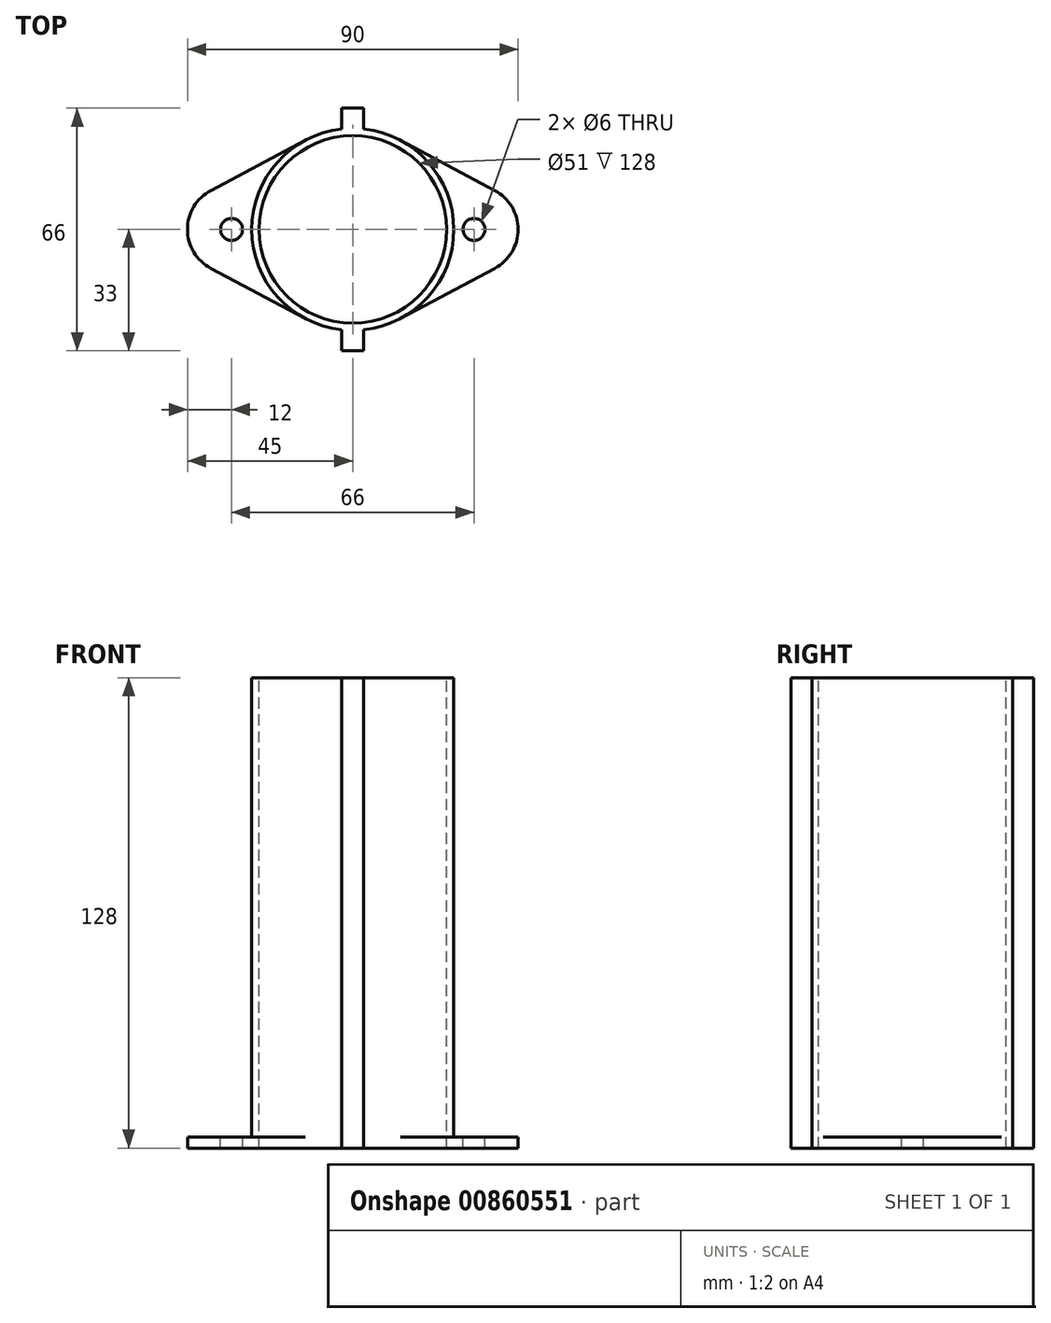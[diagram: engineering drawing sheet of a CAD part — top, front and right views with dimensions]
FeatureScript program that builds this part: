
annotation { "Feature Type Name" : "Feature", "Feature Type Description" : "" }
export const myFeature = defineFeature(function(context is Context, id is Id, definition is map)
    precondition{}
    {
        {
            var Q0;
            Q0=qCreatedBy(makeId("Top.planeOp"),FACE);
            var sketch = newSketch(context, id + "F0", { "sketchPlane" : qUnion([Q0])});
            skPoint(sketch, "E0", {"position": v(-33, 0) * mm});
            skPoint(sketch, "E1", {"position": v(33, 0) * mm});
            skCircle(sketch, "E2", {"center": v(-33, 0) * mm, "radius": 3 * mm});
            skCircle(sketch, "E3", {"center": v(33, 0) * mm, "radius": 3 * mm});
            skCircle(sketch, "E4", {"center": v(0, 0) * mm, "radius": 27.5 * mm});
            skCircle(sketch, "E5", {"center": v(-33, 0) * mm, "radius": 12 * mm});
            skCircle(sketch, "E6", {"center": v(33, 0) * mm, "radius": 12 * mm});
            skLineSegment(sketch, "E7", {"start": v(-44.55, 7.45) * mm, "end": v(-7.38, 27.22) * mm});
            skLineSegment(sketch, "E8", {"start": v(8.05, 26.87) * mm, "end": v(44.27, 7.6) * mm});
            skLineSegment(sketch, "E9", {"start": v(-44.37, -7.54) * mm, "end": v(-9.32, -26.19) * mm});
            skLineSegment(sketch, "E10", {"start": v(44, -7.74) * mm, "end": v(9.39, -26.15) * mm});
            skCircle(sketch, "E11", {"center": v(0, 0) * mm, "radius": 25.5 * mm});
            skLineSegment(sketch, "E12.bottom", {"start": v(-3, 33) * mm, "end": v(3, 33) * mm});
            skLineSegment(sketch, "E12.top", {"start": v(-3, -33) * mm, "end": v(3, -33) * mm});
            skLineSegment(sketch, "E12.left", {"start": v(-3, 33) * mm, "end": v(-3, -33) * mm});
            skLineSegment(sketch, "E12.right", {"start": v(3, 33) * mm, "end": v(3, -33) * mm});
            skSolve(sketch);
        }
        {
            var Q0;
            {var subQ0=sQuery(id+"F0.wireOp",EDGE,"E8");var subQ1=sQuery(id+"F0.wireOp",EDGE,"E4");var subQ2=makeQuery(id+"F0.imprint","INTERSECT",VERTEX,{"derivedFrom":[subQ1,subQ0]});Q0=makeQuery(id+"F0.imprint","IMPRINT",FACE,{"disambiguationData":[TD([[makeQuery(id+"F0.imprint","IMPRINT",EDGE,{"disambiguationData":[TD([[subQ2,1.0]])],"derivedFrom":subQ1}),-1.0]])]});}
            var Q1;
            Q1=makeQuery(id+"F0.imprint","IMPRINT",FACE,{"disambiguationData":[TD([[makeQuery(id+"F0.imprint","IMPRINT",EDGE,{"derivedFrom":sQuery(id+"F0.wireOp",EDGE,"E3")}),-1.0]])]});
            var Q2;
            {var subQ0=sQuery(id+"F0.wireOp",EDGE,"E6");var subQ1=sQuery(id+"F0.wireOp",EDGE,"E4");var subQ2=makeQuery(id+"F0.imprint","INTERSECT",VERTEX,{"disambiguationData":[OD(0.0)],"derivedFrom":[subQ1,subQ0]});Q2=makeQuery(id+"F0.imprint","IMPRINT",FACE,{"disambiguationData":[TD([[makeQuery(id+"F0.imprint","IMPRINT",EDGE,{"disambiguationData":[TD([[subQ2,1.0]])],"derivedFrom":subQ1}),1.0]])]});}
            var Q3;
            {var subQ10=sQuery(id+"F0.wireOp",EDGE,"E12.bottom");Q3=makeQuery(id+"F0.imprint","IMPRINT",FACE,{"disambiguationData":[TD([[makeQuery(id+"F0.imprint","IMPRINT",EDGE,{"derivedFrom":subQ10}),1.0]])]});}
            var Q4;
            {var subQ0=sQuery(id+"F0.wireOp",EDGE,"E10");var subQ1=sQuery(id+"F0.wireOp",EDGE,"E4");var subQ2=makeQuery(id+"F0.imprint","INTERSECT",VERTEX,{"derivedFrom":[subQ1,subQ0]});Q4=makeQuery(id+"F0.imprint","IMPRINT",FACE,{"disambiguationData":[TD([[makeQuery(id+"F0.imprint","IMPRINT",EDGE,{"disambiguationData":[TD([[subQ2,-1.0]])],"derivedFrom":subQ1}),-1.0]])]});}
            var Q5;
            {var subQ1=sQuery(id+"F0.wireOp",EDGE,"uCnmd3xf-1DHz-8HX0-QWDX-xBedthpKxEkq.bottom");Q5=makeQuery(id+"F0.imprint","IMPRINT",FACE,{"disambiguationData":[TD([[makeQuery(id+"F0.imprint","IMPRINT",EDGE,{"derivedFrom":subQ1}),1.0]])]});}
            var Q6;
            {var subQ0=sQuery(id+"F0.wireOp",EDGE,"E12.left");var subQ1=sQuery(id+"F0.wireOp",EDGE,"W2dtvIMr-H2jL-05E6-sB4P-pdGcn9n6LOdG");var subQ2=makeQuery(id+"F0.imprint","INTERSECT",VERTEX,{"disambiguationData":[OD(0.0)],"derivedFrom":[subQ1,subQ0]});Q6=makeQuery(id+"F0.imprint","IMPRINT",FACE,{"disambiguationData":[TD([[makeQuery(id+"F0.imprint","IMPRINT",EDGE,{"disambiguationData":[TD([[subQ2,-1.0]])],"derivedFrom":subQ1}),-1.0]])]});}
            var Q7;
            {var subQ5=sQuery(id+"F0.wireOp",EDGE,"uCnmd3xf-1DHz-8HX0-QWDX-xBedthpKxEkq.bottom");Q7=makeQuery(id+"F0.imprint","IMPRINT",FACE,{"disambiguationData":[TD([[makeQuery(id+"F0.imprint","IMPRINT",EDGE,{"derivedFrom":subQ5}),-1.0]])]});}
            var Q8;
            {var subQ0=sQuery(id+"F0.wireOp",EDGE,"uCnmd3xf-1DHz-8HX0-QWDX-xBedthpKxEkq.right");var subQ1=sQuery(id+"F0.wireOp",EDGE,"W2dtvIMr-H2jL-05E6-sB4P-pdGcn9n6LOdG");var subQ2=makeQuery(id+"F0.imprint","INTERSECT",VERTEX,{"disambiguationData":[OD(0.0)],"derivedFrom":[subQ1,subQ0]});Q8=makeQuery(id+"F0.imprint","IMPRINT",FACE,{"disambiguationData":[TD([[makeQuery(id+"F0.imprint","IMPRINT",EDGE,{"disambiguationData":[TD([[subQ2,-1.0]])],"derivedFrom":subQ1}),-1.0]])]});}
            var Q9;
            {var subQ0=sQuery(id+"F0.wireOp",EDGE,"uCnmd3xf-1DHz-8HX0-QWDX-xBedthpKxEkq.left");var subQ1=sQuery(id+"F0.wireOp",EDGE,"W2dtvIMr-H2jL-05E6-sB4P-pdGcn9n6LOdG");var subQ2=makeQuery(id+"F0.imprint","INTERSECT",VERTEX,{"disambiguationData":[OD(0.0)],"derivedFrom":[subQ1,subQ0]});Q9=makeQuery(id+"F0.imprint","IMPRINT",FACE,{"disambiguationData":[TD([[makeQuery(id+"F0.imprint","IMPRINT",EDGE,{"disambiguationData":[TD([[subQ2,-1.0]])],"derivedFrom":subQ1}),-1.0]])]});}
            var Q10;
            {var subQ0=sQuery(id+"F0.wireOp",EDGE,"82vNiPyT-JWAm-ZdGo-BXKd-8rWHJqwmHx42.bottom");var subQ1=sQuery(id+"F0.wireOp",EDGE,"W2dtvIMr-H2jL-05E6-sB4P-pdGcn9n6LOdG");var subQ2=makeQuery(id+"F0.imprint","INTERSECT",VERTEX,{"disambiguationData":[OD(0.0)],"derivedFrom":[subQ1,subQ0]});Q10=makeQuery(id+"F0.imprint","IMPRINT",FACE,{"disambiguationData":[TD([[makeQuery(id+"F0.imprint","IMPRINT",EDGE,{"disambiguationData":[TD([[subQ2,-1.0]])],"derivedFrom":subQ1}),-1.0]])]});}
            var Q11;
            {var subQ0=sQuery(id+"F0.wireOp",EDGE,"E12.right");var subQ1=sQuery(id+"F0.wireOp",EDGE,"W2dtvIMr-H2jL-05E6-sB4P-pdGcn9n6LOdG");var subQ2=makeQuery(id+"F0.imprint","INTERSECT",VERTEX,{"disambiguationData":[OD(0.0)],"derivedFrom":[subQ1,subQ0]});Q11=makeQuery(id+"F0.imprint","IMPRINT",FACE,{"disambiguationData":[TD([[makeQuery(id+"F0.imprint","IMPRINT",EDGE,{"disambiguationData":[TD([[subQ2,-1.0]])],"derivedFrom":subQ1}),-1.0]])]});}
            var Q12;
            {var subQ0=sQuery(id+"F0.wireOp",EDGE,"82vNiPyT-JWAm-ZdGo-BXKd-8rWHJqwmHx42.bottom");var subQ1=sQuery(id+"F0.wireOp",EDGE,"W2dtvIMr-H2jL-05E6-sB4P-pdGcn9n6LOdG");var subQ2=makeQuery(id+"F0.imprint","INTERSECT",VERTEX,{"disambiguationData":[OD(1.0)],"derivedFrom":[subQ1,subQ0]});Q12=makeQuery(id+"F0.imprint","IMPRINT",FACE,{"disambiguationData":[TD([[makeQuery(id+"F0.imprint","IMPRINT",EDGE,{"disambiguationData":[TD([[subQ2,-1.0]])],"derivedFrom":subQ1}),-1.0]])]});}
            var Q13;
            {var subQ0=sQuery(id+"F0.wireOp",EDGE,"kkNvgBHZ-zSj7-8Lj1-WI96-c3132SsyxNSe.bottom");var subQ1=sQuery(id+"F0.wireOp",EDGE,"W2dtvIMr-H2jL-05E6-sB4P-pdGcn9n6LOdG");var subQ2=makeQuery(id+"F0.imprint","INTERSECT",VERTEX,{"disambiguationData":[OD(1.0)],"derivedFrom":[subQ1,subQ0]});Q13=makeQuery(id+"F0.imprint","IMPRINT",FACE,{"disambiguationData":[TD([[makeQuery(id+"F0.imprint","IMPRINT",EDGE,{"disambiguationData":[TD([[subQ2,-1.0]])],"derivedFrom":subQ1}),-1.0]])]});}
            var Q14;
            {var subQ5=sQuery(id+"F0.wireOp",EDGE,"kkNvgBHZ-zSj7-8Lj1-WI96-c3132SsyxNSe.left");Q14=makeQuery(id+"F0.imprint","IMPRINT",FACE,{"disambiguationData":[TD([[makeQuery(id+"F0.imprint","IMPRINT",EDGE,{"derivedFrom":subQ5}),1.0]])]});}
            var Q15;
            {var subQ0=sQuery(id+"F0.wireOp",EDGE,"kkNvgBHZ-zSj7-8Lj1-WI96-c3132SsyxNSe.left");Q15=makeQuery(id+"F0.imprint","IMPRINT",FACE,{"disambiguationData":[TD([[makeQuery(id+"F0.imprint","IMPRINT",EDGE,{"derivedFrom":subQ0}),-1.0]])]});}
            var Q16;
            {var subQ0=sQuery(id+"F0.wireOp",EDGE,"kkNvgBHZ-zSj7-8Lj1-WI96-c3132SsyxNSe.top");var subQ1=sQuery(id+"F0.wireOp",EDGE,"W2dtvIMr-H2jL-05E6-sB4P-pdGcn9n6LOdG");var subQ2=makeQuery(id+"F0.imprint","INTERSECT",VERTEX,{"disambiguationData":[OD(0.0)],"derivedFrom":[subQ1,subQ0]});Q16=makeQuery(id+"F0.imprint","IMPRINT",FACE,{"disambiguationData":[TD([[makeQuery(id+"F0.imprint","IMPRINT",EDGE,{"disambiguationData":[TD([[subQ2,-1.0]])],"derivedFrom":subQ1}),-1.0]])]});}
            var Q17;
            {var subQ0=sQuery(id+"F0.wireOp",EDGE,"kkNvgBHZ-zSj7-8Lj1-WI96-c3132SsyxNSe.right");Q17=makeQuery(id+"F0.imprint","IMPRINT",FACE,{"disambiguationData":[TD([[makeQuery(id+"F0.imprint","IMPRINT",EDGE,{"derivedFrom":subQ0}),1.0]])]});}
            var Q18;
            {var subQ0=sQuery(id+"F0.wireOp",EDGE,"82vNiPyT-JWAm-ZdGo-BXKd-8rWHJqwmHx42.bottom");var subQ1=sQuery(id+"F0.wireOp",EDGE,"W2dtvIMr-H2jL-05E6-sB4P-pdGcn9n6LOdG");var subQ2=makeQuery(id+"F0.imprint","INTERSECT",VERTEX,{"disambiguationData":[OD(0.0)],"derivedFrom":[subQ1,subQ0]});Q18=makeQuery(id+"F0.imprint","IMPRINT",FACE,{"disambiguationData":[TD([[makeQuery(id+"F0.imprint","IMPRINT",EDGE,{"disambiguationData":[TD([[subQ2,1.0]])],"derivedFrom":subQ1}),-1.0]])]});}
            var Q19;
            {var subQ0=sQuery(id+"F0.wireOp",EDGE,"kkNvgBHZ-zSj7-8Lj1-WI96-c3132SsyxNSe.bottom");var subQ1=sQuery(id+"F0.wireOp",EDGE,"W2dtvIMr-H2jL-05E6-sB4P-pdGcn9n6LOdG");var subQ2=makeQuery(id+"F0.imprint","INTERSECT",VERTEX,{"disambiguationData":[OD(0.0)],"derivedFrom":[subQ1,subQ0]});Q19=makeQuery(id+"F0.imprint","IMPRINT",FACE,{"disambiguationData":[TD([[makeQuery(id+"F0.imprint","IMPRINT",EDGE,{"disambiguationData":[TD([[subQ2,1.0]])],"derivedFrom":subQ1}),-1.0]])]});}
            var Q20;
            {var subQ5=sQuery(id+"F0.wireOp",EDGE,"kkNvgBHZ-zSj7-8Lj1-WI96-c3132SsyxNSe.right");Q20=makeQuery(id+"F0.imprint","IMPRINT",FACE,{"disambiguationData":[TD([[makeQuery(id+"F0.imprint","IMPRINT",EDGE,{"derivedFrom":subQ5}),-1.0]])]});}
            var Q21;
            {var subQ0=sQuery(id+"F0.wireOp",EDGE,"82vNiPyT-JWAm-ZdGo-BXKd-8rWHJqwmHx42.top");var subQ1=sQuery(id+"F0.wireOp",EDGE,"W2dtvIMr-H2jL-05E6-sB4P-pdGcn9n6LOdG");var subQ2=makeQuery(id+"F0.imprint","INTERSECT",VERTEX,{"disambiguationData":[OD(1.0)],"derivedFrom":[subQ1,subQ0]});Q21=makeQuery(id+"F0.imprint","IMPRINT",FACE,{"disambiguationData":[TD([[makeQuery(id+"F0.imprint","IMPRINT",EDGE,{"disambiguationData":[TD([[subQ2,-1.0]])],"derivedFrom":subQ1}),-1.0]])]});}
            var Q22;
            {var subQ0=sQuery(id+"F0.wireOp",EDGE,"E12.right");var subQ1=sQuery(id+"F0.wireOp",EDGE,"W2dtvIMr-H2jL-05E6-sB4P-pdGcn9n6LOdG");var subQ2=makeQuery(id+"F0.imprint","INTERSECT",VERTEX,{"disambiguationData":[OD(1.0)],"derivedFrom":[subQ1,subQ0]});Q22=makeQuery(id+"F0.imprint","IMPRINT",FACE,{"disambiguationData":[TD([[makeQuery(id+"F0.imprint","IMPRINT",EDGE,{"disambiguationData":[TD([[subQ2,-1.0]])],"derivedFrom":subQ1}),-1.0]])]});}
            var Q23;
            {var subQ0=sQuery(id+"F0.wireOp",EDGE,"82vNiPyT-JWAm-ZdGo-BXKd-8rWHJqwmHx42.top");var subQ1=sQuery(id+"F0.wireOp",EDGE,"W2dtvIMr-H2jL-05E6-sB4P-pdGcn9n6LOdG");var subQ2=makeQuery(id+"F0.imprint","INTERSECT",VERTEX,{"disambiguationData":[OD(0.0)],"derivedFrom":[subQ1,subQ0]});Q23=makeQuery(id+"F0.imprint","IMPRINT",FACE,{"disambiguationData":[TD([[makeQuery(id+"F0.imprint","IMPRINT",EDGE,{"disambiguationData":[TD([[subQ2,-1.0]])],"derivedFrom":subQ1}),-1.0]])]});}
            var Q24;
            {var subQ0=sQuery(id+"F0.wireOp",EDGE,"uCnmd3xf-1DHz-8HX0-QWDX-xBedthpKxEkq.right");var subQ1=sQuery(id+"F0.wireOp",EDGE,"W2dtvIMr-H2jL-05E6-sB4P-pdGcn9n6LOdG");var subQ2=makeQuery(id+"F0.imprint","INTERSECT",VERTEX,{"disambiguationData":[OD(1.0)],"derivedFrom":[subQ1,subQ0]});Q24=makeQuery(id+"F0.imprint","IMPRINT",FACE,{"disambiguationData":[TD([[makeQuery(id+"F0.imprint","IMPRINT",EDGE,{"disambiguationData":[TD([[subQ2,-1.0]])],"derivedFrom":subQ1}),-1.0]])]});}
            var Q25;
            {var subQ0=sQuery(id+"F0.wireOp",EDGE,"uCnmd3xf-1DHz-8HX0-QWDX-xBedthpKxEkq.left");var subQ1=sQuery(id+"F0.wireOp",EDGE,"W2dtvIMr-H2jL-05E6-sB4P-pdGcn9n6LOdG");var subQ2=makeQuery(id+"F0.imprint","INTERSECT",VERTEX,{"disambiguationData":[OD(1.0)],"derivedFrom":[subQ1,subQ0]});Q25=makeQuery(id+"F0.imprint","IMPRINT",FACE,{"disambiguationData":[TD([[makeQuery(id+"F0.imprint","IMPRINT",EDGE,{"disambiguationData":[TD([[subQ2,-1.0]])],"derivedFrom":subQ1}),-1.0]])]});}
            var Q26;
            {var subQ0=sQuery(id+"F0.wireOp",EDGE,"E12.left");var subQ1=sQuery(id+"F0.wireOp",EDGE,"W2dtvIMr-H2jL-05E6-sB4P-pdGcn9n6LOdG");var subQ2=makeQuery(id+"F0.imprint","INTERSECT",VERTEX,{"disambiguationData":[OD(1.0)],"derivedFrom":[subQ1,subQ0]});Q26=makeQuery(id+"F0.imprint","IMPRINT",FACE,{"disambiguationData":[TD([[makeQuery(id+"F0.imprint","IMPRINT",EDGE,{"disambiguationData":[TD([[subQ2,-1.0]])],"derivedFrom":subQ1}),-1.0]])]});}
            var Q27;
            {var subQ1=sQuery(id+"F0.wireOp",EDGE,"uCnmd3xf-1DHz-8HX0-QWDX-xBedthpKxEkq.top");Q27=makeQuery(id+"F0.imprint","IMPRINT",FACE,{"disambiguationData":[TD([[makeQuery(id+"F0.imprint","IMPRINT",EDGE,{"derivedFrom":subQ1}),-1.0]])]});}
            var Q28;
            {var subQ5=sQuery(id+"F0.wireOp",EDGE,"uCnmd3xf-1DHz-8HX0-QWDX-xBedthpKxEkq.top");Q28=makeQuery(id+"F0.imprint","IMPRINT",FACE,{"disambiguationData":[TD([[makeQuery(id+"F0.imprint","IMPRINT",EDGE,{"derivedFrom":subQ5}),1.0]])]});}
            var Q29;
            {var subQ0=sQuery(id+"F0.wireOp",EDGE,"E7");var subQ1=sQuery(id+"F0.wireOp",EDGE,"E4");var subQ2=makeQuery(id+"F0.imprint","INTERSECT",VERTEX,{"derivedFrom":[subQ1,subQ0]});Q29=makeQuery(id+"F0.imprint","IMPRINT",FACE,{"disambiguationData":[TD([[makeQuery(id+"F0.imprint","IMPRINT",EDGE,{"disambiguationData":[TD([[subQ2,-1.0]])],"derivedFrom":subQ1}),-1.0]])]});}
            var Q30;
            Q30=makeQuery(id+"F0.imprint","IMPRINT",FACE,{"disambiguationData":[TD([[makeQuery(id+"F0.imprint","IMPRINT",EDGE,{"derivedFrom":sQuery(id+"F0.wireOp",EDGE,"E2")}),-1.0]])]});
            var Q31;
            {var subQ0=sQuery(id+"F0.wireOp",EDGE,"E5");var subQ1=sQuery(id+"F0.wireOp",EDGE,"E4");var subQ2=makeQuery(id+"F0.imprint","INTERSECT",VERTEX,{"disambiguationData":[OD(0.0)],"derivedFrom":[subQ1,subQ0]});Q31=makeQuery(id+"F0.imprint","IMPRINT",FACE,{"disambiguationData":[TD([[makeQuery(id+"F0.imprint","IMPRINT",EDGE,{"disambiguationData":[TD([[subQ2,-1.0]])],"derivedFrom":subQ1}),1.0]])]});}
            var Q32;
            {var subQ0=sQuery(id+"F0.wireOp",EDGE,"E9");var subQ1=sQuery(id+"F0.wireOp",EDGE,"E4");var subQ2=makeQuery(id+"F0.imprint","INTERSECT",VERTEX,{"derivedFrom":[subQ1,subQ0]});Q32=makeQuery(id+"F0.imprint","IMPRINT",FACE,{"disambiguationData":[TD([[makeQuery(id+"F0.imprint","IMPRINT",EDGE,{"disambiguationData":[TD([[subQ2,1.0]])],"derivedFrom":subQ1}),-1.0]])]});}
            var Q33;
            {var subQ5=sQuery(id+"F0.wireOp",EDGE,"E12.bottom");Q33=makeQuery(id+"F0.imprint","IMPRINT",FACE,{"disambiguationData":[TD([[makeQuery(id+"F0.imprint","IMPRINT",EDGE,{"derivedFrom":subQ5}),-1.0]])]});}
            var Q34;
            {var subQ0=sQuery(id+"F0.wireOp",EDGE,"E12.right");var subQ1=sQuery(id+"F0.wireOp",EDGE,"E4");var subQ2=makeQuery(id+"F0.imprint","INTERSECT",VERTEX,{"disambiguationData":[OD(0.0)],"derivedFrom":[subQ1,subQ0]});Q34=makeQuery(id+"F0.imprint","IMPRINT",FACE,{"disambiguationData":[TD([[makeQuery(id+"F0.imprint","IMPRINT",EDGE,{"disambiguationData":[TD([[subQ2,-1.0]])],"derivedFrom":subQ1}),1.0]])]});}
            var Q35;
            {var subQ0=sQuery(id+"F0.wireOp",EDGE,"E4");var subQ4=makeQuery(id+"F0.imprint","INTERSECT",VERTEX,{"derivedFrom":[subQ0,sQuery(id+"F0.wireOp",EDGE,"E8")]});Q35=makeQuery(id+"F0.imprint","IMPRINT",FACE,{"disambiguationData":[TD([[makeQuery(id+"F0.imprint","IMPRINT",EDGE,{"disambiguationData":[TD([[subQ4,1.0]])],"derivedFrom":subQ0}),1.0]])]});}
            var Q36;
            {var subQ0=sQuery(id+"F0.wireOp",EDGE,"E4");var subQ6=makeQuery(id+"F0.imprint","INTERSECT",VERTEX,{"derivedFrom":[subQ0,sQuery(id+"F0.wireOp",EDGE,"E7")]});Q36=makeQuery(id+"F0.imprint","IMPRINT",FACE,{"disambiguationData":[TD([[makeQuery(id+"F0.imprint","IMPRINT",EDGE,{"disambiguationData":[TD([[subQ6,1.0]])],"derivedFrom":subQ0}),1.0]])]});}
            var Q37;
            {var subQ0=sQuery(id+"F0.wireOp",EDGE,"E12.left");var subQ1=sQuery(id+"F0.wireOp",EDGE,"E4");var subQ2=makeQuery(id+"F0.imprint","INTERSECT",VERTEX,{"disambiguationData":[OD(1.0)],"derivedFrom":[subQ1,subQ0]});Q37=makeQuery(id+"F0.imprint","IMPRINT",FACE,{"disambiguationData":[TD([[makeQuery(id+"F0.imprint","IMPRINT",EDGE,{"disambiguationData":[TD([[subQ2,-1.0]])],"derivedFrom":subQ1}),1.0]])]});}
            var Q38;
            {var subQ5=sQuery(id+"F0.wireOp",EDGE,"E12.top");Q38=makeQuery(id+"F0.imprint","IMPRINT",FACE,{"disambiguationData":[TD([[makeQuery(id+"F0.imprint","IMPRINT",EDGE,{"derivedFrom":subQ5}),1.0]])]});}
            var Q39;
            {var subQ1=sQuery(id+"F0.wireOp",EDGE,"E4");var subQ5=makeQuery(id+"F0.imprint","INTERSECT",VERTEX,{"derivedFrom":[subQ1,sQuery(id+"F0.wireOp",EDGE,"E10")]});Q39=makeQuery(id+"F0.imprint","IMPRINT",FACE,{"disambiguationData":[TD([[makeQuery(id+"F0.imprint","IMPRINT",EDGE,{"disambiguationData":[TD([[subQ5,1.0]])],"derivedFrom":subQ1}),1.0]])]});}
            var Q40;
            {var subQ5=sQuery(id+"F0.wireOp",EDGE,"E4");var subQ6=makeQuery(id+"F0.imprint","INTERSECT",VERTEX,{"derivedFrom":[subQ5,sQuery(id+"F0.wireOp",EDGE,"E9")]});Q40=makeQuery(id+"F0.imprint","IMPRINT",FACE,{"disambiguationData":[TD([[makeQuery(id+"F0.imprint","IMPRINT",EDGE,{"disambiguationData":[TD([[subQ6,1.0]])],"derivedFrom":subQ5}),1.0]])]});}
            extrude(context, id + "F1", {"entities" : qUnion([Q0, Q1, Q2, Q3, Q4, Q5, Q6, Q7, Q8, Q9, Q10, Q11, Q12, Q13, Q14, Q15, Q16, Q17, Q18, Q19, Q20, Q21, Q22, Q23, Q24, Q25, Q26, Q27, Q28, Q29, Q30, Q31, Q32, Q33, Q34, Q35, Q36, Q37, Q38, Q39, Q40]), "oppositeDirection" : true, "depth" : 3 * mm, "offsetDistance" : 25 * mm});
        }
        {
            var Q0;
            {var subQ0=sQuery(id+"F0.wireOp",EDGE,"E4");var subQ6=makeQuery(id+"F0.imprint","INTERSECT",VERTEX,{"derivedFrom":[subQ0,sQuery(id+"F0.wireOp",EDGE,"E7")]});Q0=makeQuery(id+"F0.imprint","IMPRINT",FACE,{"disambiguationData":[TD([[makeQuery(id+"F0.imprint","IMPRINT",EDGE,{"disambiguationData":[TD([[subQ6,1.0]])],"derivedFrom":subQ0}),1.0]])]});}
            var Q1;
            {var subQ5=sQuery(id+"F0.wireOp",EDGE,"E12.bottom");Q1=makeQuery(id+"F0.imprint","IMPRINT",FACE,{"disambiguationData":[TD([[makeQuery(id+"F0.imprint","IMPRINT",EDGE,{"derivedFrom":subQ5}),-1.0]])]});}
            var Q2;
            {var subQ0=sQuery(id+"F0.wireOp",EDGE,"E12.right");var subQ1=sQuery(id+"F0.wireOp",EDGE,"E4");var subQ2=makeQuery(id+"F0.imprint","INTERSECT",VERTEX,{"disambiguationData":[OD(0.0)],"derivedFrom":[subQ1,subQ0]});Q2=makeQuery(id+"F0.imprint","IMPRINT",FACE,{"disambiguationData":[TD([[makeQuery(id+"F0.imprint","IMPRINT",EDGE,{"disambiguationData":[TD([[subQ2,-1.0]])],"derivedFrom":subQ1}),1.0]])]});}
            var Q3;
            {var subQ0=sQuery(id+"F0.wireOp",EDGE,"E4");var subQ4=makeQuery(id+"F0.imprint","INTERSECT",VERTEX,{"derivedFrom":[subQ0,sQuery(id+"F0.wireOp",EDGE,"E8")]});Q3=makeQuery(id+"F0.imprint","IMPRINT",FACE,{"disambiguationData":[TD([[makeQuery(id+"F0.imprint","IMPRINT",EDGE,{"disambiguationData":[TD([[subQ4,1.0]])],"derivedFrom":subQ0}),1.0]])]});}
            var Q4;
            {var subQ5=sQuery(id+"F0.wireOp",EDGE,"E12.top");Q4=makeQuery(id+"F0.imprint","IMPRINT",FACE,{"disambiguationData":[TD([[makeQuery(id+"F0.imprint","IMPRINT",EDGE,{"derivedFrom":subQ5}),1.0]])]});}
            var Q5;
            {var subQ0=sQuery(id+"F0.wireOp",EDGE,"E5");var subQ1=sQuery(id+"F0.wireOp",EDGE,"E4");var subQ2=makeQuery(id+"F0.imprint","INTERSECT",VERTEX,{"disambiguationData":[OD(0.0)],"derivedFrom":[subQ1,subQ0]});Q5=makeQuery(id+"F0.imprint","IMPRINT",FACE,{"disambiguationData":[TD([[makeQuery(id+"F0.imprint","IMPRINT",EDGE,{"disambiguationData":[TD([[subQ2,-1.0]])],"derivedFrom":subQ1}),1.0]])]});}
            var Q6;
            {var subQ0=sQuery(id+"F0.wireOp",EDGE,"E6");var subQ1=sQuery(id+"F0.wireOp",EDGE,"E4");var subQ2=makeQuery(id+"F0.imprint","INTERSECT",VERTEX,{"disambiguationData":[OD(0.0)],"derivedFrom":[subQ1,subQ0]});Q6=makeQuery(id+"F0.imprint","IMPRINT",FACE,{"disambiguationData":[TD([[makeQuery(id+"F0.imprint","IMPRINT",EDGE,{"disambiguationData":[TD([[subQ2,1.0]])],"derivedFrom":subQ1}),1.0]])]});}
            var Q7;
            {var subQ0=sQuery(id+"F0.wireOp",EDGE,"E12.left");var subQ1=sQuery(id+"F0.wireOp",EDGE,"E4");var subQ2=makeQuery(id+"F0.imprint","INTERSECT",VERTEX,{"disambiguationData":[OD(1.0)],"derivedFrom":[subQ1,subQ0]});Q7=makeQuery(id+"F0.imprint","IMPRINT",FACE,{"disambiguationData":[TD([[makeQuery(id+"F0.imprint","IMPRINT",EDGE,{"disambiguationData":[TD([[subQ2,-1.0]])],"derivedFrom":subQ1}),1.0]])]});}
            var Q8;
            {var subQ5=sQuery(id+"F0.wireOp",EDGE,"E4");var subQ6=makeQuery(id+"F0.imprint","INTERSECT",VERTEX,{"derivedFrom":[subQ5,sQuery(id+"F0.wireOp",EDGE,"E9")]});Q8=makeQuery(id+"F0.imprint","IMPRINT",FACE,{"disambiguationData":[TD([[makeQuery(id+"F0.imprint","IMPRINT",EDGE,{"disambiguationData":[TD([[subQ6,1.0]])],"derivedFrom":subQ5}),1.0]])]});}
            var Q9;
            {var subQ1=sQuery(id+"F0.wireOp",EDGE,"E4");var subQ5=makeQuery(id+"F0.imprint","INTERSECT",VERTEX,{"derivedFrom":[subQ1,sQuery(id+"F0.wireOp",EDGE,"E10")]});Q9=makeQuery(id+"F0.imprint","IMPRINT",FACE,{"disambiguationData":[TD([[makeQuery(id+"F0.imprint","IMPRINT",EDGE,{"disambiguationData":[TD([[subQ5,1.0]])],"derivedFrom":subQ1}),1.0]])]});}
            extrude(context, id + "F2", {"entities" : qUnion([Q0, Q1, Q2, Q3, Q4, Q5, Q6, Q7, Q8, Q9]), "operationType" : NewBodyOperationType.ADD, "depth" : 125 * mm, "offsetDistance" : 25 * mm});
        }
    });
